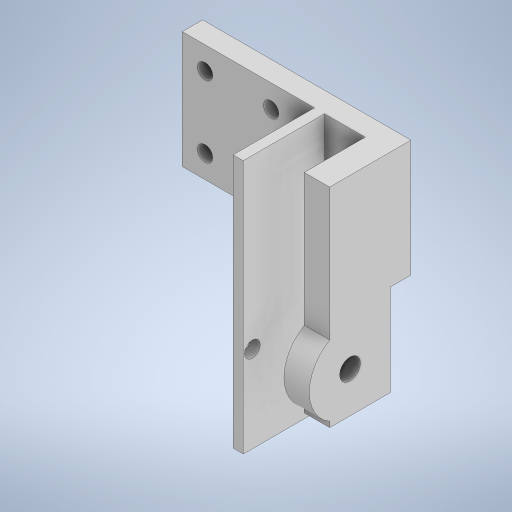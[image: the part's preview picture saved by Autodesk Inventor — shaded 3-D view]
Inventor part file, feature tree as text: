
AUTODESK INVENTOR PART (.ipt)
format: ipt  version: 2024.2 (Build 282272000, 272)  size: 306,176 bytes
history: native  units: mm
features: other x8, extrude x7, sketch x5, reference x4, thread x1, projected_geometry x1
ambient origin geometry x8: Origin, YZ Plane, XZ Plane, XY Plane, X Axis, Y Axis, Z Axis, Center Point
bodies: Body1 (feature_tree)
feature tree (26):
  other  "Твердое тело1"
  other  "РабПлоскость1"
  extrude  "Выдавливание1"  Depth=18.0mm
  sketch  "Эскиз2"
  extrude  "Выдавливание2"  Depth=18.0mm
  extrude  "Выдавливание3"  Depth=14.0mm
  thread  "Резьба1"
  extrude  "Выдавливание4"  Depth=3.0mm
  sketch  "Эскиз4"
  extrude  "Выдавливание5"  Depth=3.0mm
  extrude  "Выдавливание6"  Depth=3.0mm
  extrude  "Выдавливание7"  Depth=3.0mm
  sketch  "Эскиз1"
  reference  "Ссылка1"
  reference  "Ссылка2"
  reference  "Ссылка3"
  reference  "Ссылка4"
  sketch  "Эскиз3"
  sketch  "Эскиз5"
  projected_geometry  "Спроецированная петля2"
  other  "<userpath>\Documents\Artist\3D\Робот.iam"
  other  "Робот.iam"
  other  "боковая стенка:1"
  other  "NEMA17 42-40:2"
  other  "Нижняя крышка:1"
  other  "передняя стенка:2"
